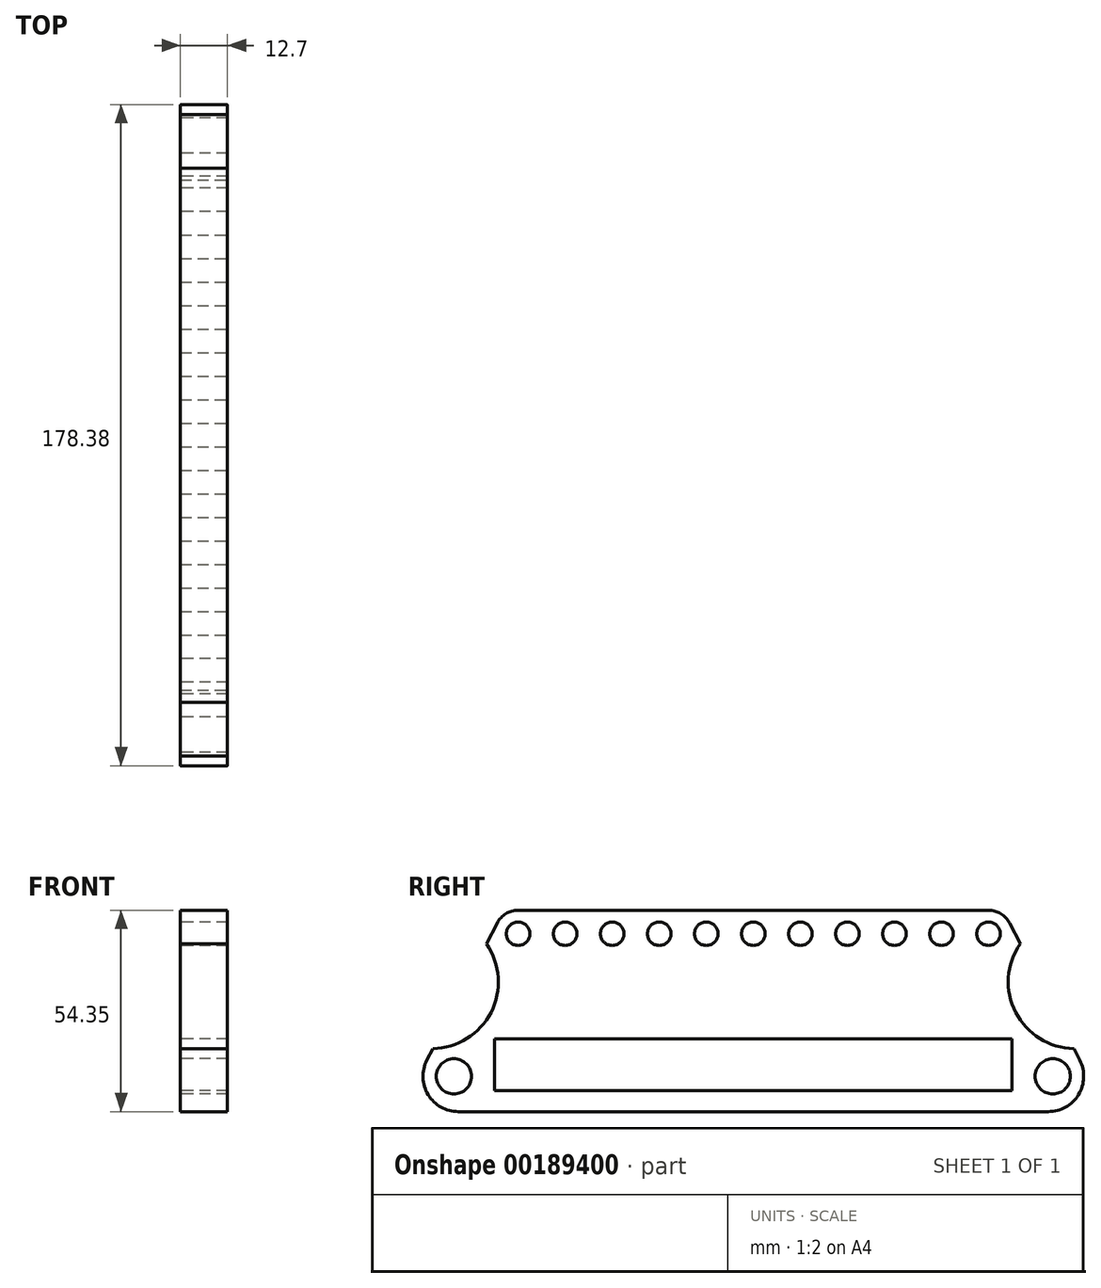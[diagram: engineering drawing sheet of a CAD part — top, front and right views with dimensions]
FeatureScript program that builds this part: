
annotation { "Feature Type Name" : "Feature", "Feature Type Description" : "" }
export const myFeature = defineFeature(function(context is Context, id is Id, definition is map)
    precondition{}
    {
        {
            var Q0;
            Q0=qCreatedBy(makeId("Right.planeOp"),FACE);
            var sketch = newSketch(context, id + "F0", { "sketchPlane" : qUnion([Q0])});
            skLineSegment(sketch, "E0.bottom", {"start": v(79.66, -12.7) * mm, "end": v(-79.66, -12.7) * mm});
            skLineSegment(sketch, "E0.left", {"start": v(88.14, 1.17) * mm, "end": v(69.15, 38.2) * mm});
            skLineSegment(sketch, "E0.right", {"start": v(-88.14, 1.17) * mm, "end": v(-69.15, 38.2) * mm});
            skPoint(sketch, "E0.middle", {"position": v(0, 0) * mm});
            skCircle(sketch, "E1", {"center": v(80.84, -3.17) * mm, "radius": 4.76 * mm});
            skCircle(sketch, "E2", {"center": v(-80.84, -3.17) * mm, "radius": 4.76 * mm});
            skLineSegment(sketch, "E3.bottom", {"start": v(69.85, -6.99) * mm, "end": v(-69.85, -6.99) * mm});
            skLineSegment(sketch, "E3.top", {"start": v(69.85, 6.99) * mm, "end": v(-69.85, 6.98) * mm});
            skLineSegment(sketch, "E3.left", {"start": v(69.85, -6.99) * mm, "end": v(69.85, 6.99) * mm});
            skLineSegment(sketch, "E3.right", {"start": v(-69.85, -6.99) * mm, "end": v(-69.85, 6.99) * mm});
            skLineSegment(sketch, "E4", {"start": v(80.84, -3.17) * mm, "end": v(90.37, -3.17) * mm, "construction": true});
            skLineSegment(sketch, "E5", {"start": v(-80.84, -3.17) * mm, "end": v(-90.37, -3.17) * mm, "construction": true});
            skPoint(sketch, "E6.visualSharp", {"position": v(-95.25, -12.7) * mm});
            skArc(sketch, "E6.filletArc", {"start": v(-88.14, 1.17) * mm, "mid": v(-87.79, -8.14) * mm, "end": v(-79.66, -12.7) * mm});
            skPoint(sketch, "E7.visualSharp", {"position": v(95.25, -12.7) * mm});
            skArc(sketch, "E7.filletArc", {"start": v(79.66, -12.7) * mm, "mid": v(87.79, -8.14) * mm, "end": v(88.14, 1.17) * mm});
            skLineSegment(sketch, "E8", {"start": v(-63.5, 41.65) * mm, "end": v(63.5, 41.65) * mm});
            skPoint(sketch, "E9.visualSharp", {"position": v(-67.38, 41.65) * mm});
            skArc(sketch, "E9.filletArc", {"start": v(-63.5, 41.65) * mm, "mid": v(-66.81, 40.72) * mm, "end": v(-69.15, 38.2) * mm});
            skPoint(sketch, "E10.visualSharp", {"position": v(67.38, 41.65) * mm});
            skArc(sketch, "E10.filletArc", {"start": v(69.15, 38.2) * mm, "mid": v(66.81, 40.72) * mm, "end": v(63.5, 41.65) * mm});
            skCircle(sketch, "E11", {"center": v(-63.5, 35.3) * mm, "radius": 3.18 * mm});
            skCircle(sketch, "E12", {"center": v(63.5, 35.3) * mm, "radius": 3.18 * mm});
            skLineSegment(sketch, "E13", {"start": v(0, 41.65) * mm, "end": v(0, -12.7) * mm, "construction": true});
            skPoint(sketch, "E14", {"position": v(-78.64, 19.69) * mm});
            skPoint(sketch, "E15", {"position": v(78.64, 19.68) * mm});
            skSolve(sketch);
        }
        {
            var Q0;
            Q0=qSketchRegion(id+"F0",true);
            extrude(context, id + "F1", {"entities" : qUnion([Q0]), "offsetDistance" : 25.4 * mm, "depth" : 12.7 * mm});
        }
        {
            var Q0;
            Q0=makeQuery(id+"F1.opExtrude","CAP_FACE",FACE,{"disambiguationData":[OSD([sQuery(id+"F0.wireOp",EDGE,"E0.bottom"),sQuery(id+"F0.wireOp",EDGE,"E0.left"),sQuery(id+"F0.wireOp",EDGE,"E0.right"),sQuery(id+"F0.wireOp",EDGE,"E1"),sQuery(id+"F0.wireOp",EDGE,"E2"),sQuery(id+"F0.wireOp",EDGE,"E3.bottom"),sQuery(id+"F0.wireOp",EDGE,"E3.top"),sQuery(id+"F0.wireOp",EDGE,"E3.left"),sQuery(id+"F0.wireOp",EDGE,"E3.right"),sQuery(id+"F0.wireOp",EDGE,"E6.filletArc"),sQuery(id+"F0.wireOp",EDGE,"E7.filletArc"),sQuery(id+"F0.wireOp",EDGE,"E8"),sQuery(id+"F0.wireOp",EDGE,"E9.filletArc"),sQuery(id+"F0.wireOp",EDGE,"E10.filletArc"),sQuery(id+"F0.wireOp",EDGE,"E11"),sQuery(id+"F0.wireOp",EDGE,"E12")])],"isStart":false});
            var sketch = newSketch(context, id + "F2", { "sketchPlane" : qUnion([Q0])});
            skLineSegment(sketch, "E16", {"start": v(0, -12.7) * mm, "end": v(0, 41.65) * mm, "construction": true});
            skArc(sketch, "E17", {"start": v(-86.53, 4.3) * mm, "mid": v(-70.82, 14.08) * mm, "end": v(-72.05, 32.55) * mm});
            skArc(sketch, "E18.MirrorCS", {"start": v(86.53, 4.3) * mm, "mid": v(70.82, 14.08) * mm, "end": v(72.05, 32.55) * mm});
            skLineSegment(sketch, "E19", {"start": v(-72.05, 32.55) * mm, "end": v(-86.53, 4.3) * mm});
            skLineSegment(sketch, "E20.MirrorCS", {"start": v(72.05, 32.55) * mm, "end": v(86.53, 4.3) * mm});
            skSolve(sketch);
        }
        {
            var Q0;
            Q0 = qSketchRegion(id + "F2", true);
            extrude(context, id + "F3", {"entities" : qUnion([Q0]), "operationType" : NewBodyOperationType.REMOVE, "oppositeDirection" : true, "depth" : 25.4 * mm, "offsetDistance" : 25.4 * mm});
        }
        {
            var Q0;
            Q0=makeQuery(id+"F1.opExtrude","CAP_FACE",FACE,{"disambiguationData":[OSD([sQuery(id+"F0.wireOp",EDGE,"E0.bottom"),sQuery(id+"F0.wireOp",EDGE,"E0.left"),sQuery(id+"F0.wireOp",EDGE,"E0.right"),sQuery(id+"F0.wireOp",EDGE,"E1"),sQuery(id+"F0.wireOp",EDGE,"E2"),sQuery(id+"F0.wireOp",EDGE,"E3.bottom"),sQuery(id+"F0.wireOp",EDGE,"E3.top"),sQuery(id+"F0.wireOp",EDGE,"E3.left"),sQuery(id+"F0.wireOp",EDGE,"E3.right"),sQuery(id+"F0.wireOp",EDGE,"E6.filletArc"),sQuery(id+"F0.wireOp",EDGE,"E7.filletArc"),sQuery(id+"F0.wireOp",EDGE,"E8"),sQuery(id+"F0.wireOp",EDGE,"E9.filletArc"),sQuery(id+"F0.wireOp",EDGE,"E10.filletArc"),sQuery(id+"F0.wireOp",EDGE,"E11"),sQuery(id+"F0.wireOp",EDGE,"E12")])],"isStart":false});
            var sketch = newSketch(context, id + "F4", { "sketchPlane" : qUnion([Q0])});
            skLineSegment(sketch, "E21", {"start": v(-63.5, 35.3) * mm, "end": v(63.5, 35.3) * mm, "construction": true});
            skCircle(sketch, "E22", {"center": v(-50.8, 35.3) * mm, "radius": 3.18 * mm});
            skCircle(sketch, "E23.1.0.0", {"center": v(-38.1, 35.3) * mm, "radius": 3.18 * mm});
            skCircle(sketch, "E23.2.0.0", {"center": v(-25.4, 35.3) * mm, "radius": 3.18 * mm});
            skCircle(sketch, "E23.3.0.0", {"center": v(-12.7, 35.3) * mm, "radius": 3.18 * mm});
            skCircle(sketch, "E23.4.0.0", {"center": v(0, 35.3) * mm, "radius": 3.18 * mm});
            skCircle(sketch, "E23.5.0.0", {"center": v(12.7, 35.3) * mm, "radius": 3.18 * mm});
            skCircle(sketch, "E23.6.0.0", {"center": v(25.4, 35.3) * mm, "radius": 3.18 * mm});
            skCircle(sketch, "E23.7.0.0", {"center": v(38.1, 35.3) * mm, "radius": 3.18 * mm});
            skLineSegment(sketch, "E23.direction1", {"start": v(-50.8, 35.3) * mm, "end": v(-38.1, 35.3) * mm, "construction": true});
            skCircle(sketch, "E24.0.8.0", {"center": v(50.8, 35.3) * mm, "radius": 3.18 * mm});
            skCircle(sketch, "E24.0.9.0", {"center": v(63.5, 35.3) * mm, "radius": 3.18 * mm});
            skSolve(sketch);
        }
        {
            var Q0;
            Q0 = qSketchRegion(id + "F4", true);
            extrude(context, id + "F5", {"entities" : qUnion([Q0]), "operationType" : NewBodyOperationType.REMOVE, "oppositeDirection" : true, "depth" : 25.4 * mm, "offsetDistance" : 25.4 * mm});
        }
    });
